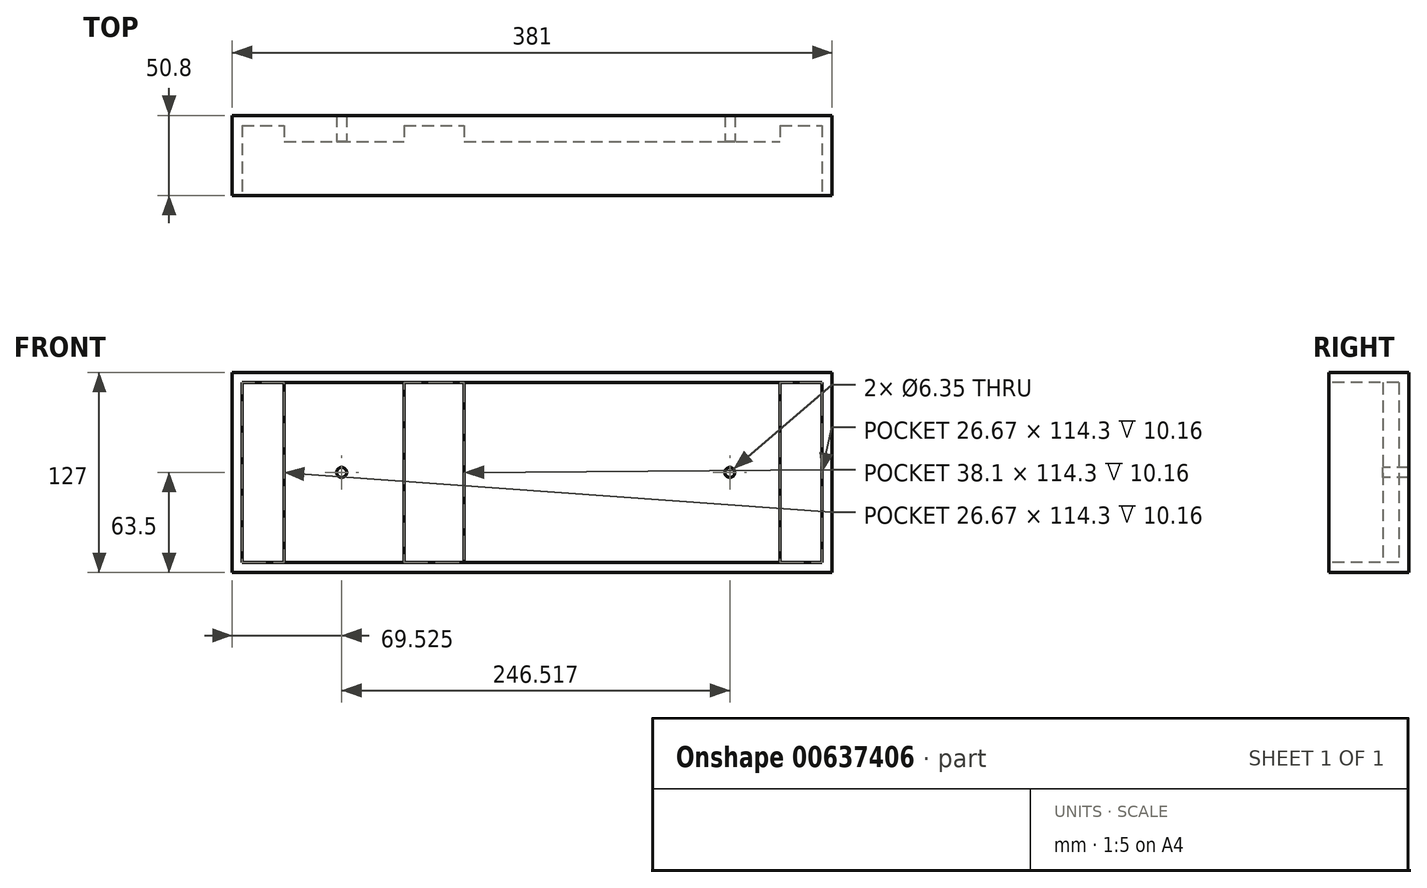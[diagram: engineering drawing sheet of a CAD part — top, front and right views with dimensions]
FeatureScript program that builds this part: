
annotation { "Feature Type Name" : "Feature", "Feature Type Description" : "" }
export const myFeature = defineFeature(function(context is Context, id is Id, definition is map)
    precondition{}
    {
        {
            var Q0;
            Q0=qCreatedBy(makeId("Front.planeOp"),FACE);
            var sketch = newSketch(context, id + "F0", { "sketchPlane" : qUnion([Q0])});
            skLineSegment(sketch, "E0", {"start": v(0, 0) * mm, "end": v(0, 127) * mm});
            skLineSegment(sketch, "E1", {"start": v(0, 0) * mm, "end": v(381, 0) * mm});
            skLineSegment(sketch, "E2", {"start": v(0, 127) * mm, "end": v(381, 127) * mm});
            skLineSegment(sketch, "E3", {"start": v(381, 127) * mm, "end": v(381, 0) * mm});
            skSolve(sketch);
        }
        {
            var Q0;
            Q0 = qSketchRegion(id + "F0", true);
            extrude(context, id + "F1", {"entities" : qUnion([Q0]), "depth" : 50.8 * mm, "offsetDistance" : 25.4 * mm});
        }
        {
            var Q0;
            Q0=makeQuery(id+"F1.opExtrude","CAP_FACE",FACE,{"disambiguationData":[OSD([sQuery(id+"F0.wireOp",EDGE,"E0"),sQuery(id+"F0.wireOp",EDGE,"E1"),sQuery(id+"F0.wireOp",EDGE,"E2"),sQuery(id+"F0.wireOp",EDGE,"E3")])],"isStart":false});
            var sketch = newSketch(context, id + "F2", { "sketchPlane" : qUnion([Q0])});
            skLineSegment(sketch, "E4", {"start": v(6.35, 120.65) * mm, "end": v(6.35, 6.35) * mm});
            skLineSegment(sketch, "E5", {"start": v(6.35, 6.35) * mm, "end": v(374.65, 6.35) * mm});
            skLineSegment(sketch, "E6", {"start": v(6.35, 120.65) * mm, "end": v(374.65, 120.65) * mm});
            skLineSegment(sketch, "E7", {"start": v(374.65, 120.65) * mm, "end": v(374.65, 6.35) * mm});
            skLineSegment(sketch, "E8", {"start": v(33.02, 120.65) * mm, "end": v(33.02, 6.35) * mm});
            skLineSegment(sketch, "E9", {"start": v(109.22, 120.65) * mm, "end": v(109.22, 6.35) * mm});
            skLineSegment(sketch, "E10", {"start": v(147.32, 120.65) * mm, "end": v(147.32, 6.35) * mm});
            skLineSegment(sketch, "E11", {"start": v(347.98, 120.65) * mm, "end": v(347.98, 6.35) * mm});
            skSolve(sketch);
        }
        {
            var Q0;
            {var subQ0=sQuery(id+"F2.wireOp",EDGE,"E4");Q0=makeQuery(id+"F2.imprint","IMPRINT",FACE,{"disambiguationData":[TD([[makeQuery(id+"F2.imprint","IMPRINT",EDGE,{"derivedFrom":subQ0}),1.0]])]});}
            var Q1;
            {var subQ0=sQuery(id+"F2.wireOp",EDGE,"E9");Q1=makeQuery(id+"F2.imprint","IMPRINT",FACE,{"disambiguationData":[TD([[makeQuery(id+"F2.imprint","IMPRINT",EDGE,{"derivedFrom":subQ0}),1.0]])]});}
            var Q2;
            {var subQ0=sQuery(id+"F2.wireOp",EDGE,"E7");Q2=makeQuery(id+"F2.imprint","IMPRINT",FACE,{"disambiguationData":[TD([[makeQuery(id+"F2.imprint","IMPRINT",EDGE,{"derivedFrom":subQ0}),-1.0]])]});}
            extrude(context, id + "F3", {"entities" : qUnion([Q0, Q1, Q2]), "operationType" : NewBodyOperationType.REMOVE, "oppositeDirection" : true, "depth" : 44.45 * mm, "offsetDistance" : 25.4 * mm});
        }
        {
            var Q0;
            Q0=makeQuery(id+"F1.opExtrude","CAP_FACE",FACE,{"disambiguationData":[OSD([sQuery(id+"F0.wireOp",EDGE,"E0"),sQuery(id+"F0.wireOp",EDGE,"E1"),sQuery(id+"F0.wireOp",EDGE,"E2"),sQuery(id+"F0.wireOp",EDGE,"E3")])],"isStart":false});
            var sketch = newSketch(context, id + "F4", { "sketchPlane" : qUnion([Q0])});
            skLineSegment(sketch, "E12", {"start": v(33.02, 120.65) * mm, "end": v(109.22, 120.65) * mm});
            skLineSegment(sketch, "E13", {"start": v(33.02, 6.35) * mm, "end": v(109.22, 6.35) * mm});
            skLineSegment(sketch, "E14", {"start": v(147.32, 120.65) * mm, "end": v(347.98, 120.65) * mm});
            skLineSegment(sketch, "E15", {"start": v(147.32, 6.35) * mm, "end": v(347.98, 6.35) * mm});
            skSolve(sketch);
        }
        {
            var Q0;
            Q0 = qSketchRegion(id + "F4", true);
            var Q1;
            Q1=makeQuery(id+"F4.imprint","IMPRINT",FACE,{"disambiguationData":[TD([[makeQuery(id+"F4.imprint","IMPRINT",EDGE,{"derivedFrom":sQuery(id+"F4.wireOp",EDGE,"E12")}),-1.0]])]});
            var Q2;
            Q2=makeQuery(id+"F4.imprint","IMPRINT",FACE,{"disambiguationData":[TD([[makeQuery(id+"F4.imprint","IMPRINT",EDGE,{"derivedFrom":sQuery(id+"F4.wireOp",EDGE,"E14")}),-1.0]])]});
            extrude(context, id + "F5", {"entities" : qUnion([Q0, Q1, Q2]), "operationType" : NewBodyOperationType.REMOVE, "oppositeDirection" : true, "depth" : 34.3 * mm, "offsetDistance" : 25.4 * mm});
        }
        {
            var Q0;
            Q0=makeQuery(id+"F5.boolean.opBoolean","COPY",FACE,{"derivedFrom":makeQuery(id+"F5.opExtrude","CAP_FACE",FACE,{"disambiguationData":[OSD([sQuery(id+"F2.wireOp",EDGE,"E8"),sQuery(id+"F2.wireOp",EDGE,"E9"),sQuery(id+"F4.wireOp",EDGE,"E12"),sQuery(id+"F4.wireOp",EDGE,"E13")])],"isStart":false})});
            var sketch = newSketch(context, id + "F6", { "sketchPlane" : qUnion([Q0])});
            skCircle(sketch, "E16", {"center": v(69.52, 63.5) * mm, "radius": 3.18 * mm});
            skCircle(sketch, "E17", {"center": v(316.04, 63.5) * mm, "radius": 3.18 * mm});
            skSolve(sketch);
        }
        {
            var Q0;
            Q0=makeQuery(id+"F6.imprint","IMPRINT",FACE,{"disambiguationData":[TD([[makeQuery(id+"F6.imprint","IMPRINT",EDGE,{"derivedFrom":sQuery(id+"F6.wireOp",EDGE,"E16")}),1.0]])]});
            var Q1;
            Q1=makeQuery(id+"F6.imprint","IMPRINT",FACE,{"disambiguationData":[TD([[makeQuery(id+"F6.imprint","IMPRINT",EDGE,{"derivedFrom":sQuery(id+"F6.wireOp",EDGE,"E17")}),1.0]])]});
            extrude(context, id + "F7", {"entities" : qUnion([Q0, Q1]), "operationType" : NewBodyOperationType.REMOVE, "endBound" : BoundingType.THROUGH_ALL, "oppositeDirection" : true, "depth" : 25.4 * mm, "offsetDistance" : 25.4 * mm});
        }
    });
